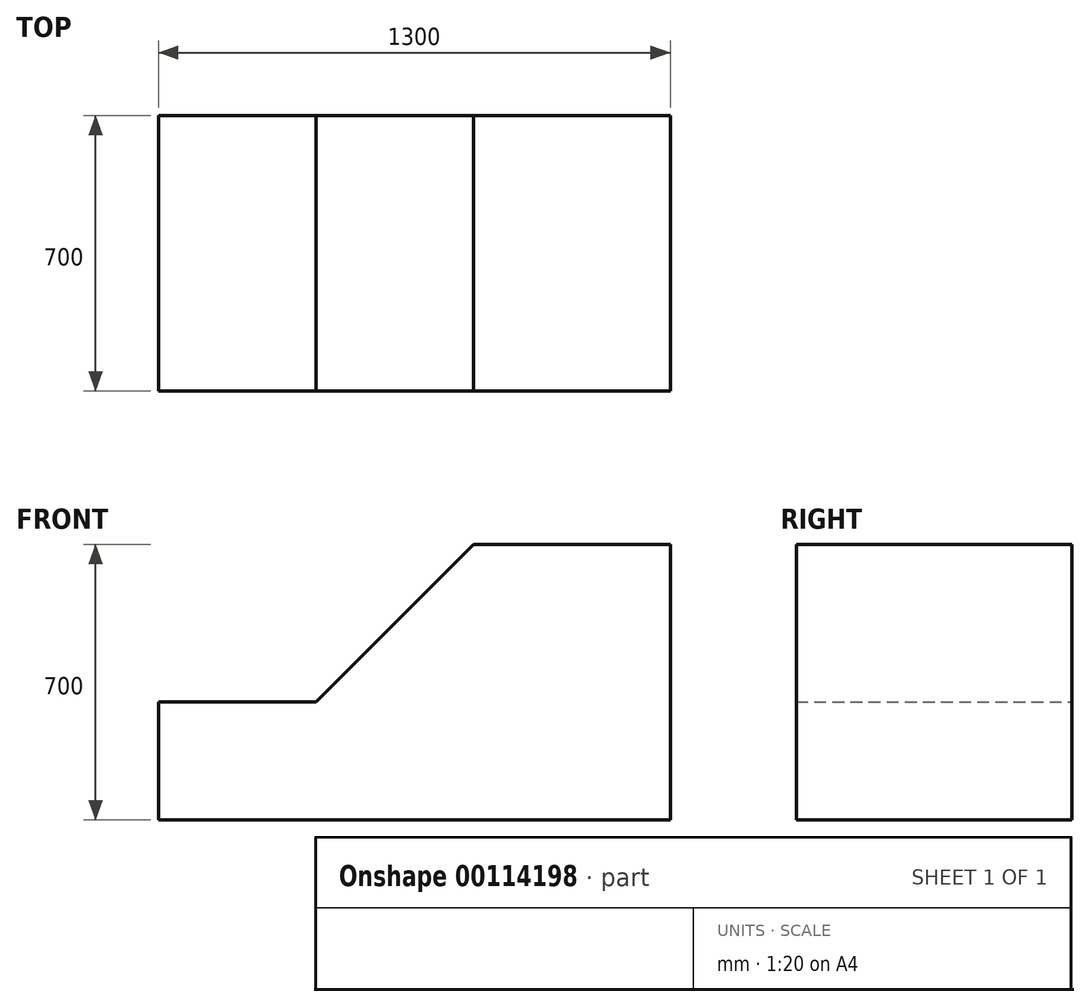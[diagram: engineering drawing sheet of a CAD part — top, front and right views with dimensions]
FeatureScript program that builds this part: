
annotation { "Feature Type Name" : "Feature", "Feature Type Description" : "" }
export const myFeature = defineFeature(function(context is Context, id is Id, definition is map)
    precondition{}
    {
        {
            var Q0;
            Q0=qCreatedBy(makeId("Front.planeOp"),FACE);
            var sketch = newSketch(context, id + "F0", { "sketchPlane" : qUnion([Q0])});
            skLineSegment(sketch, "E0.bottom", {"start": v(650, 350) * mm, "end": v(150, 350) * mm});
            skLineSegment(sketch, "E0.top", {"start": v(650, -350) * mm, "end": v(-650, -350) * mm});
            skLineSegment(sketch, "E0.left", {"start": v(650, 350) * mm, "end": v(650, -350) * mm});
            skLineSegment(sketch, "E0.right", {"start": v(-650, -50) * mm, "end": v(-650, -350) * mm});
            skPoint(sketch, "E0.middle", {"position": v(0, 0) * mm});
            skLineSegment(sketch, "E1", {"start": v(150, 350) * mm, "end": v(-250, -50) * mm});
            skLineSegment(sketch, "E2", {"start": v(-250, -50) * mm, "end": v(-650, -50) * mm});
            skPoint(sketch, "E3.orphan", {"position": v(-650, 350) * mm});
            skSolve(sketch);
        }
        {
            var Q0;
            Q0 = qSketchRegion(id + "F0", true);
            extrude(context, id + "F1", {"entities" : qUnion([Q0]), "depth" : 700 * mm});
        }
    });
